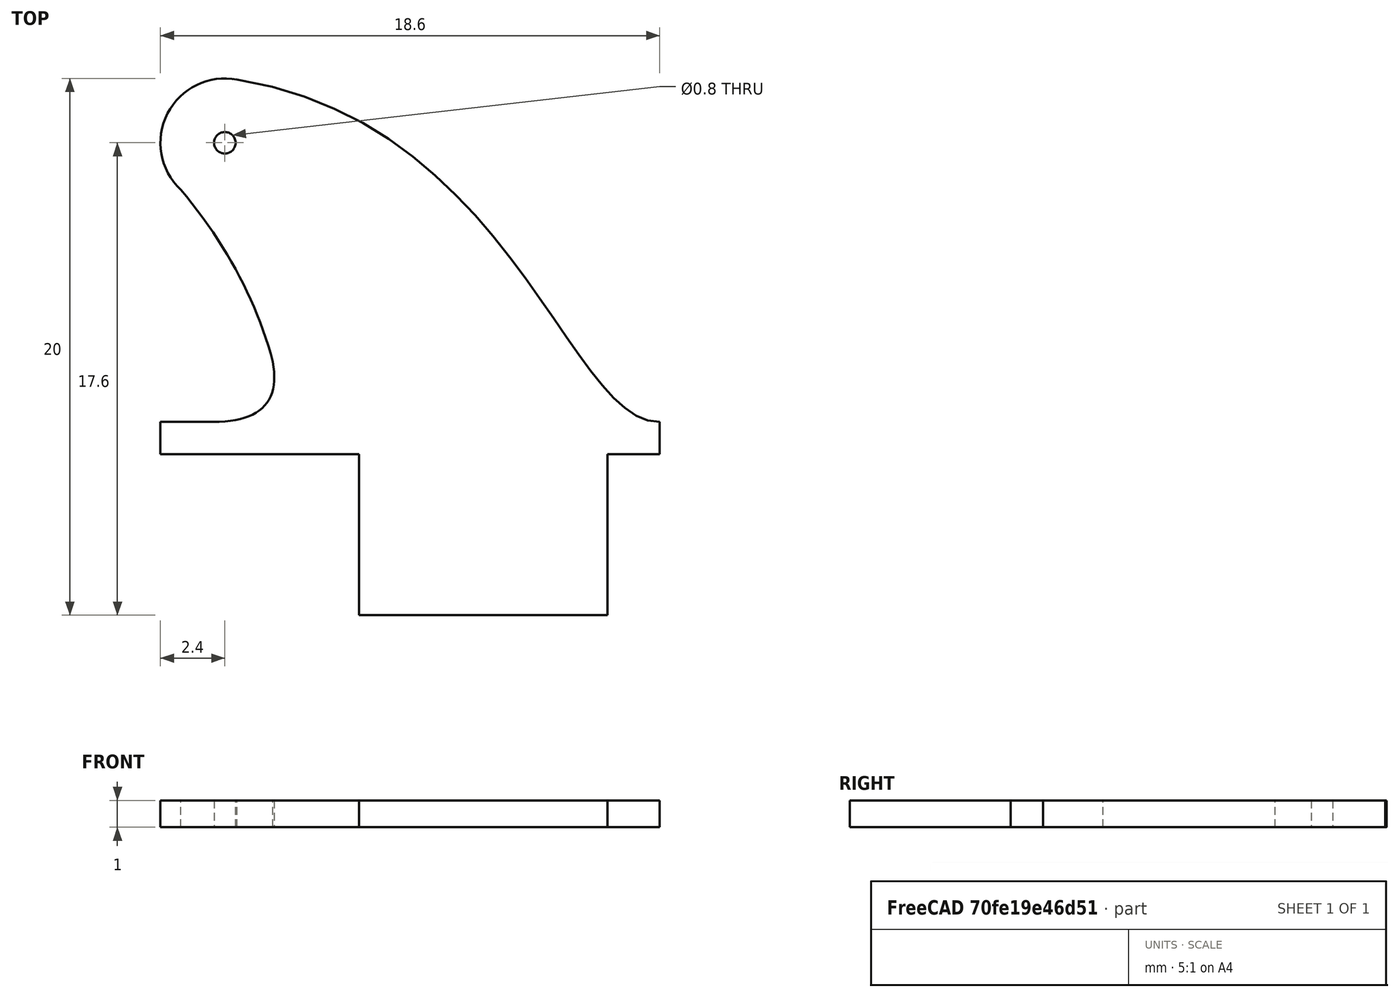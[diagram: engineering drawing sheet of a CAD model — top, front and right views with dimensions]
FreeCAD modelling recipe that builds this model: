
FCSTD DOCUMENT  (FreeCAD 0.20R0.20.2)
Label: 007
License: All rights reserved
LicenseURL: http://en.wikipedia.org/wiki/All_rights_reserved
objects: Sketcher::SketchObject×2, Part::Extrusion×1
note: 3 computed .brp shape members not serialized (recipe doc carries the construction recipe); baked Part::Feature solids carry a one-line shape summary decoded from their .brp

FEATURE [Sketcher::SketchObject] Sketch  label="main"
  FullyConstrained = true
  sketch-geometry (25):
    g0: LineSegment StartX=12.0586 StartY=-6 StartZ=0 EndX=12.0586 EndY=0 EndZ=0
    g1: LineSegment StartX=2.8 StartY=-6 StartZ=0 EndX=2.8 EndY=0 EndZ=0
    g2: LineSegment StartX=2.8 StartY=-6 StartZ=0 EndX=12.0586 EndY=-6 EndZ=0
    g3: LineSegment StartX=12.0586 StartY=0 StartZ=0 EndX=14 EndY=0 EndZ=0
    g4: LineSegment StartX=2.8 StartY=0 StartZ=0 EndX=0 EndY=0 EndZ=0
    g5: LineSegment StartX=14 StartY=0 StartZ=0 EndX=14 EndY=1.2 EndZ=0
    g6: LineSegment StartX=0 StartY=0 StartZ=0 EndX=-4.6 EndY=0 EndZ=0
    g7: Circle CenterX=-2.2 CenterY=11.6 CenterZ=0 NormalX=0 NormalY=0 NormalZ=1 AngleXU=0 Radius=0.4
    g8-g11: Circle x4 (B-spline internal-alignment scaffolding for g12; pole/knot coordinates omitted)
    g12: BSplineCurve PolesCount=4 KnotsCount=2 Degree=3 IsPeriodic=0
    g13: GeomPoint X=-1.74436 Y=13.9564 Z=0
    g14: GeomPoint X=14 Y=1.2 Z=0
    g15: ArcOfCircle CenterX=-2.2 CenterY=11.6 CenterZ=0 NormalX=0 NormalY=0 NormalZ=1 AngleXU=0 Radius=2.4 StartAngle=1.37979 EndAngle=3.95565
    g16: LineSegment StartX=-2.62672 StartY=1.2 StartZ=0 EndX=-4.6 EndY=1.2 EndZ=0
    g17: LineSegment StartX=-4.6 StartY=0 StartZ=0 EndX=-4.6 EndY=1.2 EndZ=0
    g18: Circle CenterX=-2.62672 CenterY=1.2 CenterZ=0 NormalX=0 NormalY=0 NormalZ=1 AngleXU=0 Radius=1
    g19: Circle CenterX=0 CenterY=1.2 CenterZ=0 NormalX=0 NormalY=0 NormalZ=1 AngleXU=0 Radius=1
    g20: Circle CenterX=-0.413885 CenterY=3.44541 CenterZ=0 NormalX=0 NormalY=0 NormalZ=1 AngleXU=0 Radius=1
    g21: BSplineCurve PolesCount=3 KnotsCount=2 Degree=2 IsPeriodic=0
    g22: GeomPoint X=-2.62672 Y=1.2 Z=0
    g23: GeomPoint X=-0.413885 Y=3.44541 Z=0
    g24: BSplineCurve PolesCount=3 KnotsCount=2 Degree=2 IsPeriodic=0
  constraints (52):
    c: Vertical(g0)
    c: Vertical(g1)
    c: Block(g1)
    c: Block(g0)
    c: Distance(g1) = 6
    c: Coincident(g2,g1)
    c: Horizontal(g2)
    c: Coincident(g0,g2)
    c: Block(g2)
    c: Coincident(g3,g0)
    c: Horizontal(g3)
    c: Coincident(g4,g1)
    c: Horizontal(g4)
    c: Block(g3)
    c: Block(g4)
    c: Coincident(g5,g3)
    c: Vertical(g5)
    c: Distance(g5) = 1.2
    c: Coincident(g6,g4)
    c: Horizontal(g6)
    c: Distance(g6) = 4.6
    c: Block(g7)
    c: Weight(g8) = 1
    c: Equal(g8,g9)
    c: Equal(g8,g10)
    c: Equal(g8,g11)
    c: Coincident(g12,g5)
    c: InternalAlignment(g8-g11 -> g12) x4
    c: InternalAlignment(g13,g12)
    c: InternalAlignment(g14,g12)
    c: Block(g12)
    c: Coincident(g15,g7)
    c: Coincident(g15,g12)
    c: Coincident(g15,g24)
    c: Block(g15)
    c: Horizontal(g16)
    c: Coincident(g17,g6)
    c: Vertical(g17)
    c: Coincident(g17,g16)
    c: Weight(g18) = 1
    c: Equal(g18,g19)
    c: Equal(g18,g20)
    c: InternalAlignment(g18,g21)
    c: InternalAlignment(g19,g21)
    c: InternalAlignment(g20,g21)
    c: InternalAlignment(g22,g21)
    c: InternalAlignment(g23,g21)
    c: Block(g16)
    c: Coincident(g16,g21)
    c: Coincident(g21,g24)
    c: Block(g24)
    c: Block(g21)
FEATURE [Part::Extrusion] Extrude
  Base = -> Sketch
  Dir = (0,0,1)
  DirMode = 2
  FaceMakerClass = Part::FaceMakerBullseye
  LengthFwd = 1
  LengthRev = 0
  Solid = true
  Symmetric = false
FEATURE [Sketcher::SketchObject] Sketch001  label="main001"
  FullyConstrained = false
  sketch-geometry (45):
    g0: Circle CenterX=-2.2 CenterY=11.6 CenterZ=0 NormalX=0 NormalY=0 NormalZ=1 AngleXU=0 Radius=0.4
    g1-g4: Circle x4 (B-spline internal-alignment scaffolding for g5; pole/knot coordinates omitted)
    g5: BSplineCurve PolesCount=4 KnotsCount=2 Degree=3 IsPeriodic=0
    g6: GeomPoint X=-1.74436 Y=13.9564 Z=0
    g7: GeomPoint X=14 Y=1.2 Z=0
    g8: ArcOfCircle CenterX=-2.2 CenterY=11.6 CenterZ=0 NormalX=0 NormalY=0 NormalZ=1 AngleXU=0 Radius=2.4 StartAngle=1.37979 EndAngle=3.95565
    g9: Circle CenterX=-2.62672 CenterY=1.2 CenterZ=0 NormalX=0 NormalY=0 NormalZ=1 AngleXU=0 Radius=1
    g10: Circle CenterX=0 CenterY=1.2 CenterZ=0 NormalX=0 NormalY=0 NormalZ=1 AngleXU=0 Radius=1
    g11: Circle CenterX=-0.413885 CenterY=3.44541 CenterZ=0 NormalX=0 NormalY=0 NormalZ=1 AngleXU=0 Radius=1
    g12: BSplineCurve PolesCount=3 KnotsCount=2 Degree=2 IsPeriodic=0
    g13: GeomPoint X=-2.62672 Y=1.2 Z=0
    g14: GeomPoint X=-0.413885 Y=3.44541 Z=0
    g15: BSplineCurve PolesCount=3 KnotsCount=2 Degree=2 IsPeriodic=0
    g16: Circle CenterX=1.34801 CenterY=2.51783 CenterZ=0 NormalX=0 NormalY=0 NormalZ=1 AngleXU=0 Radius=1
    g17: Circle CenterX=1.8831 CenterY=1.2 CenterZ=0 NormalX=0 NormalY=0 NormalZ=1 AngleXU=0 Radius=1
    g18: Circle CenterX=3.28198 CenterY=1.2 CenterZ=0 NormalX=0 NormalY=0 NormalZ=1 AngleXU=0 Radius=1
    g19: BSplineCurve PolesCount=3 KnotsCount=2 Degree=2 IsPeriodic=0
    g20: GeomPoint X=1.34801 Y=2.51783 Z=0
    g21: GeomPoint X=3.28198 Y=1.2 Z=0
    g22: Circle CenterX=9.22372 CenterY=2.86164 CenterZ=0 NormalX=0 NormalY=0 NormalZ=1 AngleXU=0 Radius=1
    g23: Circle CenterX=9.64409 CenterY=1.39848 CenterZ=0 NormalX=0 NormalY=0 NormalZ=1 AngleXU=0 Radius=1
    g24: Circle CenterX=7.76214 CenterY=1.2 CenterZ=0 NormalX=0 NormalY=0 NormalZ=1 AngleXU=0 Radius=1
    g25: BSplineCurve PolesCount=3 KnotsCount=2 Degree=2 IsPeriodic=0
    g26: GeomPoint X=9.22372 Y=2.86164 Z=0
    g27: GeomPoint X=7.76214 Y=1.2 Z=0
    g28: LineSegment StartX=-2.62672 StartY=1.2 StartZ=0 EndX=3.28198 EndY=1.2 EndZ=0
    g29: LineSegment StartX=7.76214 StartY=1.2 StartZ=0 EndX=14 EndY=1.2 EndZ=0
    g30: Circle CenterX=-0.671756 CenterY=12.1251 CenterZ=0 NormalX=0 NormalY=0 NormalZ=1 AngleXU=0 Radius=1
    g31: Circle CenterX=-0.754831 CenterY=12.699 CenterZ=0 NormalX=0 NormalY=0 NormalZ=1 AngleXU=0 Radius=1
    g32: Circle CenterX=0.224587 CenterY=12.4971 CenterZ=0 NormalX=0 NormalY=0 NormalZ=1 AngleXU=0 Radius=1
    g33: BSplineCurve PolesCount=3 KnotsCount=2 Degree=2 IsPeriodic=0
    g34: GeomPoint X=-0.671756 Y=12.1251 Z=0
    g35: GeomPoint X=0.224587 Y=12.4971 Z=0
    g36: Circle CenterX=-2.10085 CenterY=9.02995 CenterZ=0 NormalX=0 NormalY=0 NormalZ=1 AngleXU=0 Radius=1
    g37: Circle CenterX=-2.68572 CenterY=9.84108 CenterZ=0 NormalX=0 NormalY=0 NormalZ=1 AngleXU=0 Radius=1
    g38: Circle CenterX=-1.96262 CenterY=10.0016 CenterZ=0 NormalX=0 NormalY=0 NormalZ=1 AngleXU=0 Radius=1
    g39: BSplineCurve PolesCount=3 KnotsCount=2 Degree=2 IsPeriodic=0
    g40: GeomPoint X=-2.10085 Y=9.02995 Z=0
    g41: GeomPoint X=-1.96262 Y=10.0016 Z=0
    g42: ArcOfCircle CenterX=-2.2 CenterY=11.6 CenterZ=0 NormalX=0 NormalY=0 NormalZ=1 AngleXU=0 Radius=1.61593 StartAngle=4.85982 EndAngle=6.61413
    g43: BSplineCurve PolesCount=3 KnotsCount=2 Degree=2 IsPeriodic=0
    g44: BSplineCurve PolesCount=3 KnotsCount=2 Degree=2 IsPeriodic=0
  constraints (76):
    c: Block(g0)
    c: Weight(g1) = 1
    c: Equal(g1,g2)
    c: Equal(g1,g3)
    c: Equal(g1,g4)
    c: InternalAlignment(g1-g4 -> g5) x4
    c: InternalAlignment(g6,g5)
    c: InternalAlignment(g7,g5)
    c: Block(g5)
    c: Coincident(g8,g0)
    c: Coincident(g8,g5)
    c: Coincident(g8,g15)
    c: Block(g8)
    c: Weight(g9) = 1
    c: Equal(g9,g11)
    c: InternalAlignment(g9,g12)
    c: InternalAlignment(g10,g12)
    c: InternalAlignment(g11,g12)
    c: InternalAlignment(g13,g12)
    c: InternalAlignment(g14,g12)
    c: Coincident(g12,g15)
    c: Block(g15)
    c: Block(g12)
    c: Weight(g16) = 1
    c: Equal(g16,g17)
    c: Equal(g16,g18)
    c: InternalAlignment(g16,g19)
    c: InternalAlignment(g17,g19)
    c: InternalAlignment(g18,g19)
    c: InternalAlignment(g20,g19)
    c: InternalAlignment(g21,g19)
    c: Block(g19)
    c: Weight(g22) = 1
    c: Coincident(g25,g43)
    c: Equal(g22,g23)
    c: Equal(g22,g24)
    c: InternalAlignment(g22,g25)
    c: InternalAlignment(g23,g25)
    c: InternalAlignment(g24,g25)
    c: InternalAlignment(g26,g25)
    c: InternalAlignment(g27,g25)
    c: Block(g25)
    c: Coincident(g28,g19)
    c: Horizontal(g28)
    c: Coincident(g29,g25)
    c: Horizontal(g29)
    c: Weight(g30) = 1
    c: Equal(g30,g31)
    c: Equal(g30,g32)
    c: InternalAlignment(g30,g33)
    c: InternalAlignment(g31,g33)
    c: InternalAlignment(g32,g33)
    c: InternalAlignment(g34,g33)
    c: InternalAlignment(g35,g33)
    c: Weight(g36) = 1
    c: Equal(g36,g37)
    c: Equal(g36,g38)
    c: InternalAlignment(g36,g39)
    c: InternalAlignment(g37,g39)
    c: InternalAlignment(g38,g39)
    c: InternalAlignment(g40,g39)
    c: InternalAlignment(g41,g39)
    c: Coincident(g42,g0)
    c: Coincident(g42,g39)
    c: Coincident(g42,g33)
    c: Block(g42)
    c: PointOnObject(g43,g31)
    c: PointOnObject(g44,g37)
    c: Coincident(g33,g43)
    c: Coincident(g39,g44)
    c: Block(g43)
    c: Block(g44)
    c: Block(g39)
    c: Block(g33)
    c: Block(g29)
    c: Block(g28)
